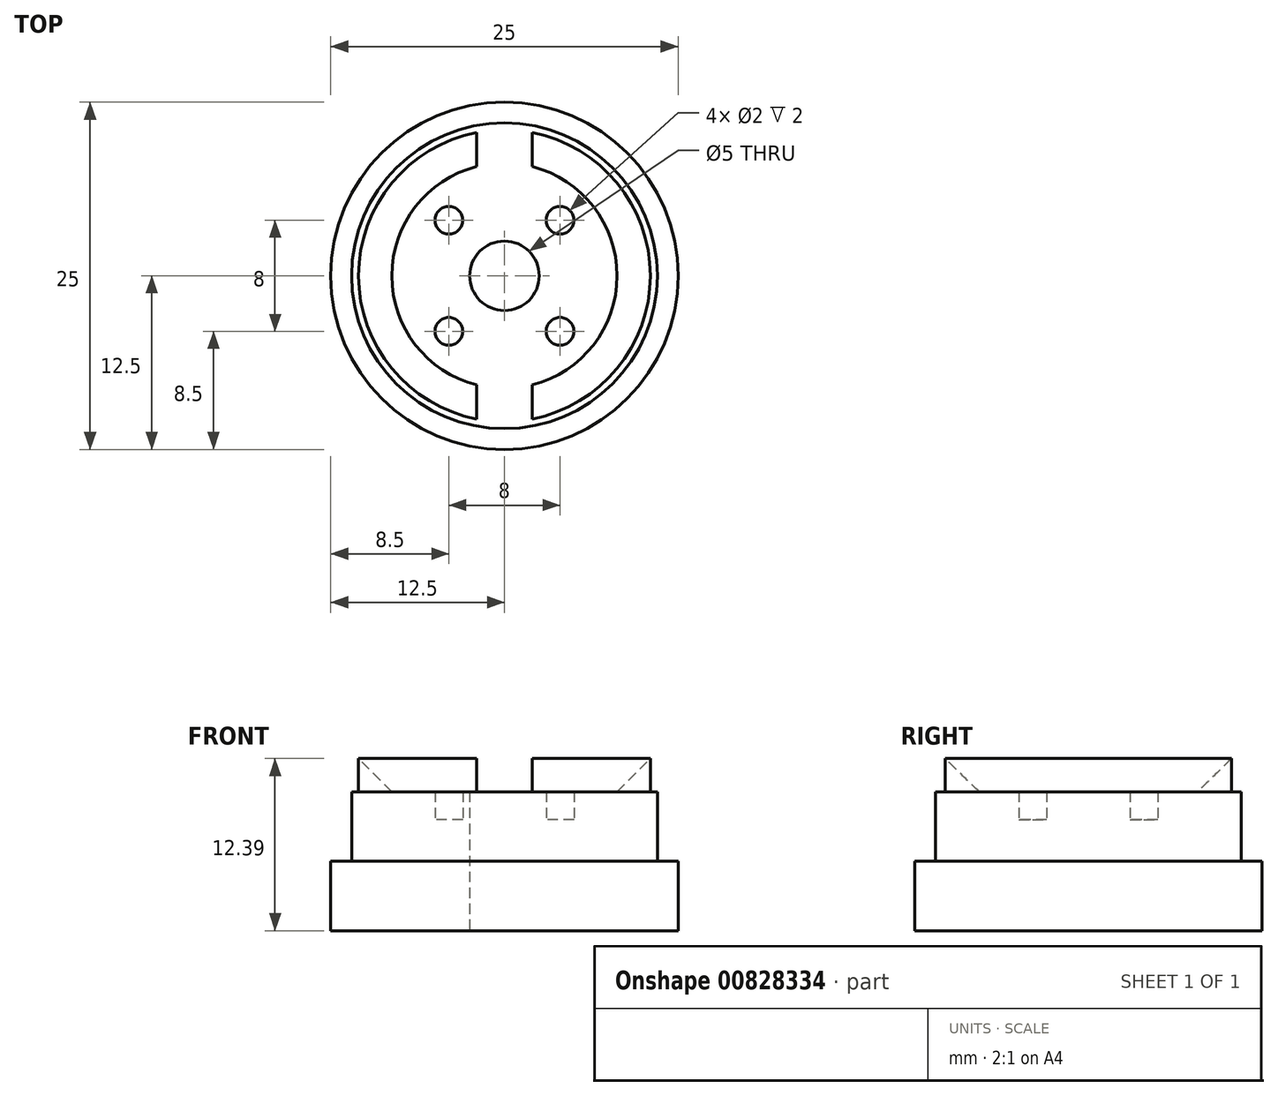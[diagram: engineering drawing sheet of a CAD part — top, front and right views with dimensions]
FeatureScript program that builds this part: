
annotation { "Feature Type Name" : "Feature", "Feature Type Description" : "" }
export const myFeature = defineFeature(function(context is Context, id is Id, definition is map)
    precondition{}
    {
        {
            var Q0;
            Q0=qCreatedBy(makeId("Top.planeOp"),FACE);
            var sketch = newSketch(context, id + "F0", { "sketchPlane" : qUnion([Q0])});
            skCircle(sketch, "E0", {"center": v(0, 0) * mm, "radius": 12.5 * mm});
            skCircle(sketch, "E1", {"center": v(0, 0) * mm, "radius": 11 * mm});
            skArc(sketch, "E2", {"start": v(-2, 10.3) * mm, "mid": v(-10.5, 0) * mm, "end": v(-2, -10.3) * mm});
            skArc(sketch, "E3", {"start": v(-2, 7.86) * mm, "mid": v(-8.1, 0) * mm, "end": v(-2, -7.86) * mm});
            skLineSegment(sketch, "E4", {"start": v(-2, -7.86) * mm, "end": v(-2, -10.3) * mm});
            skLineSegment(sketch, "E5", {"start": v(-2, -10.3) * mm, "end": v(-2, -7.86) * mm});
            skLineSegment(sketch, "E6", {"start": v(-2, 7.86) * mm, "end": v(-2, 10.3) * mm});
            skLineSegment(sketch, "E7", {"start": v(2, -10.3) * mm, "end": v(2, -7.86) * mm});
            skLineSegment(sketch, "E8.trimOffspring", {"start": v(2, 7.86) * mm, "end": v(2, 10.3) * mm});
            skArc(sketch, "E9.trimOffspring", {"start": v(2, -7.86) * mm, "mid": v(8.1, 0) * mm, "end": v(2, 7.86) * mm});
            skArc(sketch, "E10.trimOffspring", {"start": v(2, -10.3) * mm, "mid": v(10.5, 0) * mm, "end": v(2, 10.3) * mm});
            skCircle(sketch, "E11", {"center": v(-4, 4) * mm, "radius": 1 * mm});
            skCircle(sketch, "E12", {"center": v(4, 4) * mm, "radius": 1 * mm});
            skCircle(sketch, "E13", {"center": v(4, -4) * mm, "radius": 1 * mm});
            skCircle(sketch, "E14", {"center": v(-4, -4) * mm, "radius": 1 * mm});
            skSolve(sketch);
        }
        {
            var Q0;
            Q0 = qSketchRegion(id + "F0", true);
            extrude(context, id + "F1", {"entities" : qUnion([Q0]), "depth" : 5 * mm, "offsetDistance" : 25 * mm});
        }
        {
            var Q0;
            Q0=makeQuery(id+"F0.imprint","IMPRINT",FACE,{"disambiguationData":[TD([[makeQuery(id+"F0.imprint","IMPRINT",EDGE,{"derivedFrom":sQuery(id+"F0.wireOp",EDGE,"E1")}),1.0]])]});
            extrude(context, id + "F2", {"entities" : qUnion([Q0]), "operationType" : NewBodyOperationType.ADD, "depth" : 10 * mm, "offsetDistance" : 25 * mm});
        }
        {
            var Q0;
            Q0=makeQuery(id+"F0.imprint","IMPRINT",FACE,{"disambiguationData":[TD([[makeQuery(id+"F0.imprint","IMPRINT",EDGE,{"derivedFrom":sQuery(id+"F0.wireOp",EDGE,"E2")}),1.0]])]});
            var Q1;
            Q1=makeQuery(id+"F0.imprint","IMPRINT",FACE,{"disambiguationData":[TD([[makeQuery(id+"F0.imprint","IMPRINT",EDGE,{"derivedFrom":sQuery(id+"F0.wireOp",EDGE,"E7")}),-1.0]])]});
            extrude(context, id + "F3", {"entities" : qUnion([Q0, Q1]), "operationType" : NewBodyOperationType.ADD, "depth" : 15 * mm, "offsetDistance" : 25 * mm});
        }
        {
            var Q0;
            Q0=makeQuery(id+"F3.opExtrude","CAP_EDGE",EDGE,{"disambiguationData":[OSD([sQuery(id+"F0.wireOp",EDGE,"E3")])],"isStart":false});
            var Q1;
            Q1=makeQuery(id+"F3.opExtrude","CAP_EDGE",EDGE,{"disambiguationData":[OSD([sQuery(id+"F0.wireOp",EDGE,"E9.trimOffspring")])],"isStart":false});
            chamfer(context, id + "F4", {"entities" : qUnion([Q0, Q1]), "width" : 5 * mm, "tangentPropagation" : true});
        }
        {
            var Q0;
            Q0=sQuery(id+"F0.wireOp",VERTEX,"E0.center");
            var Q1;
            Q1=makeQuery(id+"F1.opExtrude","SWEPT_BODY",BODY,{"disambiguationData":[OSD([sQuery(id+"F0.wireOp",EDGE,"E0"),sQuery(id+"F0.wireOp",EDGE,"E1")])]});
            hole(context, id + "F5", {"style" : HoleStyle.SIMPLE, "endStyle" : HoleEndStyle.BLIND, "oppositeDirection" : true, "holeDiameter" : 5 * mm, "majorDiameter" : 5 * mm, "holeDepth" : 12 * mm, "isTappedThrough" : true, "tappedDepth" : 12 * mm, "tapClearance" : 3, "locations" : qUnion([Q0]), "scope" : qUnion([Q1])});
        }
        {
            var Q0;
            Q0=makeQuery(id+"F0.imprint","IMPRINT",FACE,{"disambiguationData":[TD([[makeQuery(id+"F0.imprint","IMPRINT",EDGE,{"derivedFrom":sQuery(id+"F0.wireOp",EDGE,"E11")}),1.0]])]});
            var Q1;
            Q1=makeQuery(id+"F0.imprint","IMPRINT",FACE,{"disambiguationData":[TD([[makeQuery(id+"F0.imprint","IMPRINT",EDGE,{"derivedFrom":sQuery(id+"F0.wireOp",EDGE,"E12")}),1.0]])]});
            var Q2;
            Q2=makeQuery(id+"F0.imprint","IMPRINT",FACE,{"disambiguationData":[TD([[makeQuery(id+"F0.imprint","IMPRINT",EDGE,{"derivedFrom":sQuery(id+"F0.wireOp",EDGE,"E14")}),1.0]])]});
            var Q3;
            Q3=makeQuery(id+"F0.imprint","IMPRINT",FACE,{"disambiguationData":[TD([[makeQuery(id+"F0.imprint","IMPRINT",EDGE,{"derivedFrom":sQuery(id+"F0.wireOp",EDGE,"E13")}),1.0]])]});
            extrude(context, id + "F6", {"entities" : qUnion([Q0, Q1, Q2, Q3]), "operationType" : NewBodyOperationType.ADD, "depth" : 8 * mm, "offsetDistance" : 25 * mm});
        }
    });
